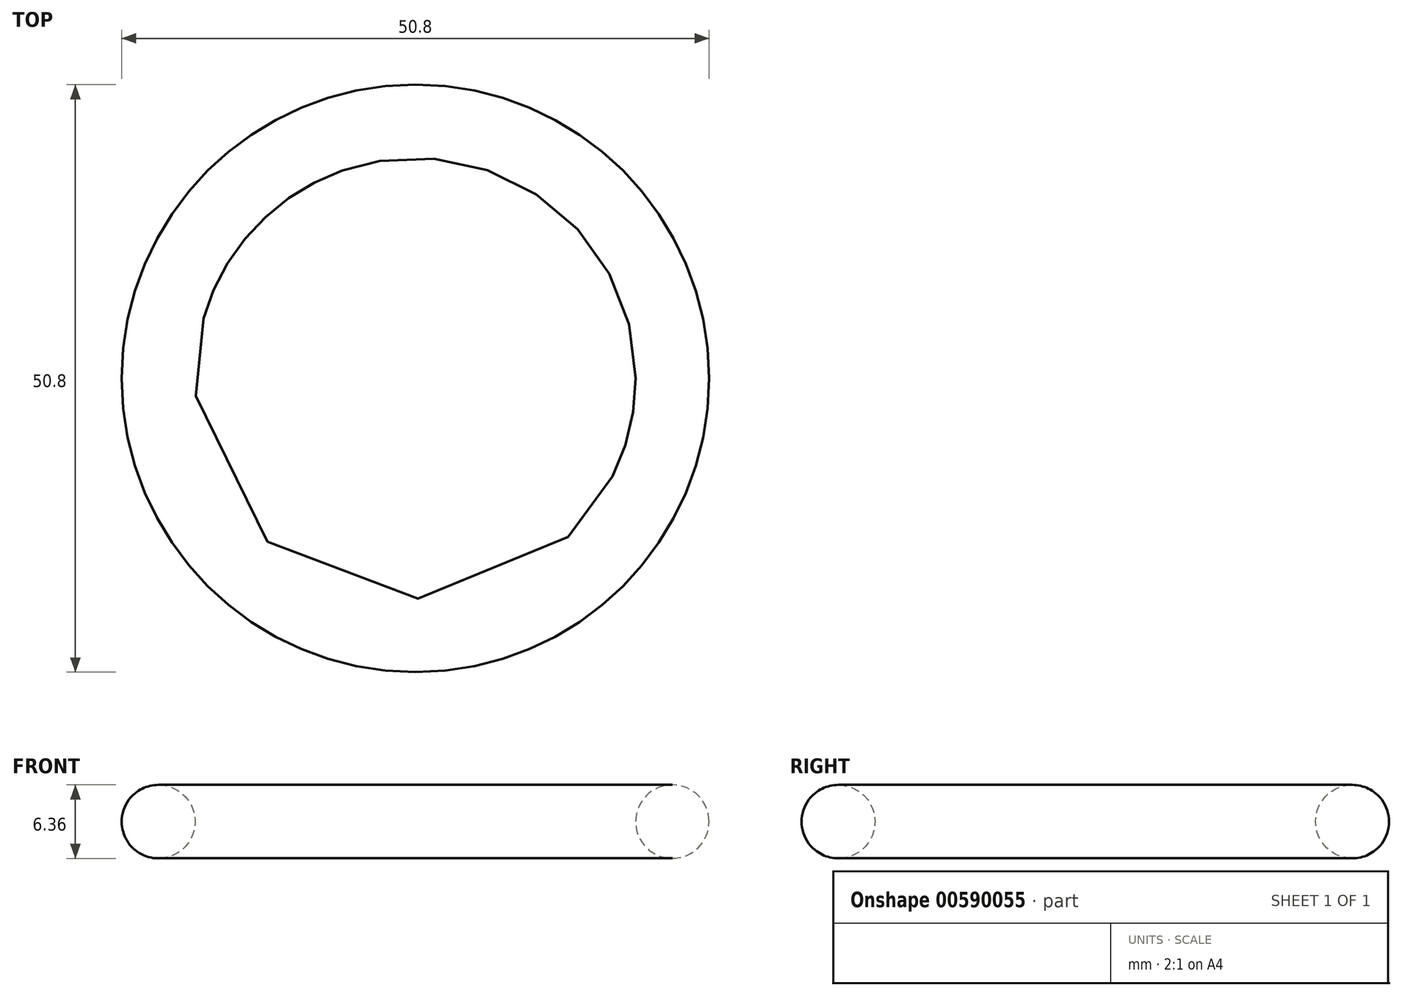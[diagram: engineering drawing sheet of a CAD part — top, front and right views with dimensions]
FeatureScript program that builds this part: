
annotation { "Feature Type Name" : "Feature", "Feature Type Description" : "" }
export const myFeature = defineFeature(function(context is Context, id is Id, definition is map)
    precondition{}
    {
        {
            var Q0;
            Q0=qCreatedBy(makeId("Front.planeOp"),FACE);
            var sketch = newSketch(context, id + "F0", { "sketchPlane" : qUnion([Q0])});
            skCircle(sketch, "E0", {"center": v(-22.23, 0) * mm, "radius": 3.18 * mm});
            skLineSegment(sketch, "E1", {"start": v(0, 10.98) * mm, "end": v(0, -17.31) * mm, "construction": true});
            skSolve(sketch);
        }
        {
            var Q0;
            Q0 = qSketchRegion(id + "F0", true);
            var Q1;
            Q1=sQuery(id+"F0.wireOp",EDGE,"E1");
            revolve(context, id + "F1", {"entities" : qUnion([Q0]), "axis" : qUnion([Q1]), "revolveType" : RevolveType.FULL});
        }
    });
